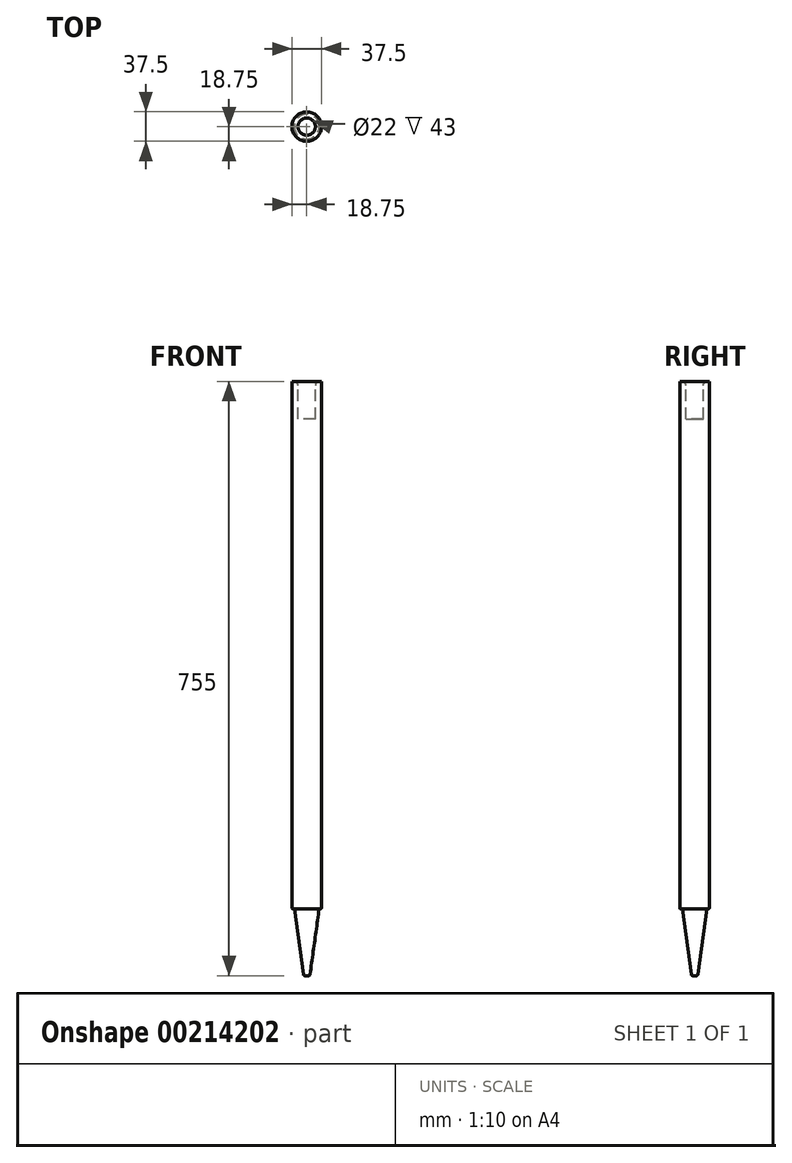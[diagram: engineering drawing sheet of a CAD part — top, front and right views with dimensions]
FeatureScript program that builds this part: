
annotation { "Feature Type Name" : "Feature", "Feature Type Description" : "" }
export const myFeature = defineFeature(function(context is Context, id is Id, definition is map)
    precondition{}
    {
        {
            var Q0;
            Q0=qCreatedBy(makeId("Front.planeOp"),FACE);
            var sketch = newSketch(context, id + "F0", { "sketchPlane" : qUnion([Q0])});
            skLineSegment(sketch, "E0", {"start": v(0, 216.86) * mm, "end": v(0, -155.63) * mm, "construction": true});
            skLineSegment(sketch, "E1", {"start": v(-16, 755) * mm, "end": v(-18.75, 755) * mm});
            skLineSegment(sketch, "E2", {"start": v(-18.75, 755) * mm, "end": v(-18.75, 86) * mm});
            skLineSegment(sketch, "E3", {"start": v(-17.75, 85) * mm, "end": v(-15.75, 85) * mm});
            skLineSegment(sketch, "E4", {"start": v(-15.75, 85) * mm, "end": v(-4.24, 1.73) * mm});
            skLineSegment(sketch, "E5", {"start": v(-2.26, 0) * mm, "end": v(0, 0) * mm});
            skLineSegment(sketch, "E6", {"start": v(-11, 750) * mm, "end": v(-11, 707) * mm});
            skLineSegment(sketch, "E7", {"start": v(-11, 707) * mm, "end": v(-6, 707) * mm});
            skLineSegment(sketch, "E8", {"start": v(0, 707) * mm, "end": v(0, 0) * mm});
            skPoint(sketch, "E9.visualSharp", {"position": v(-4, 0) * mm});
            skArc(sketch, "E9.filletArc", {"start": v(-4.24, 1.73) * mm, "mid": v(-3.57, 0.5) * mm, "end": v(-2.26, 0) * mm});
            skPoint(sketch, "E10.visualSharp", {"position": v(-18.75, 85) * mm});
            skArc(sketch, "E10.filletArc", {"start": v(-18.75, 86) * mm, "mid": v(-18.46, 85.3) * mm, "end": v(-17.75, 85) * mm});
            skLineSegment(sketch, "E11", {"start": v(-18.75, 755.5) * mm, "end": v(-18.75, 786) * mm});
            skLineSegment(sketch, "E12", {"start": v(-8.75, 796) * mm, "end": v(-1, 796) * mm});
            skLineSegment(sketch, "E13", {"start": v(-1, 796) * mm, "end": v(-1, 781.5) * mm});
            skLineSegment(sketch, "E14", {"start": v(-1, 781.5) * mm, "end": v(-6, 781.5) * mm});
            skLineSegment(sketch, "E15", {"start": v(-6, 781.5) * mm, "end": v(-6, 707.5) * mm});
            skPoint(sketch, "E16.visualSharp", {"position": v(-18.75, 796) * mm});
            skArc(sketch, "E16.filletArc", {"start": v(-8.75, 796) * mm, "mid": v(-15.82, 793.07) * mm, "end": v(-18.75, 786) * mm});
            skLineSegment(sketch, "E17", {"start": v(-6, 707.5) * mm, "end": v(-10.5, 707.5) * mm});
            skLineSegment(sketch, "E18", {"start": v(-10.5, 707.5) * mm, "end": v(-10.5, 755.5) * mm});
            skLineSegment(sketch, "E19", {"start": v(-10.5, 755.5) * mm, "end": v(-18.75, 755.5) * mm});
            skLineSegment(sketch, "E20", {"start": v(9.8, 720) * mm, "end": v(9.8, 785.5) * mm, "construction": true});
            skLineSegment(sketch, "E21", {"start": v(-1, 785.5) * mm, "end": v(9.8, 785.5) * mm, "construction": true});
            skLineSegment(sketch, "E22", {"start": v(-6, 707) * mm, "end": v(0, 707) * mm});
            skLineSegment(sketch, "E23", {"start": v(0, 707) * mm, "end": v(0, 707) * mm});
            skPoint(sketch, "E24.visualSharp", {"position": v(-11, 755) * mm});
            skArc(sketch, "E24.filletArc", {"start": v(-11, 750) * mm, "mid": v(-12.46, 753.54) * mm, "end": v(-16, 755) * mm});
            skSolve(sketch);
        }
        {
            var Q0;
            Q0=makeQuery(id+"F0.imprint","IMPRINT",FACE,{"disambiguationData":[TD([[makeQuery(id+"F0.imprint","IMPRINT",EDGE,{"derivedFrom":sQuery(id+"F0.wireOp",EDGE,"E1")}),1.0]])]});
            var Q1;
            Q1=sQuery(id+"F0.wireOp",EDGE,"E8");
            revolve(context, id + "F1", {"entities" : qUnion([Q0]), "axis" : qUnion([Q1]), "revolveType" : RevolveType.FULL});
        }
    });
